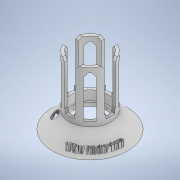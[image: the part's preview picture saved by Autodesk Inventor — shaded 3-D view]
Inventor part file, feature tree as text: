
AUTODESK INVENTOR PART (.ipt)
format: ipt  version: 2022.4 (Build 264492010, 492A)  size: 1,085,952 bytes
history: native  units: in
note: dims shown in document units (in); Inventor stores cm internally (conversion verified against a paired STEP export)
features: sketch x11, extrude x8, plane x3, pattern_circular x3, revolve x2, emboss x1
ambient origin geometry x8: Origin, YZ Plane, XZ Plane, XY Plane, X Axis, Y Axis, Z Axis, Center Point
bodies: Solid1 (feature_tree)
feature tree (28):
  extrude  "Extrusion1"  Depth=0.2559in
  plane  "Work Plane1"
  extrude  "Extrusion3"  Depth=2.3622in
  extrude  "Extrusion4"  TaperAngle=0.0deg  [1 undecoded]
  extrude  "Extrusion5"  Depth=2.2835in
  extrude  "Extrusion6"  Depth=0.1969in
  pattern_circular  "Circular Pattern2"  Count=10  [1 undecoded]
  extrude  "Extrusion7"  Depth=0.2559in
  revolve  "Revolution3"  Angle=360.0deg
  extrude  "Extrusion8"  TaperAngle=0.0deg  [1 undecoded]
  pattern_circular  "Circular Pattern4"  Count=7  [1 undecoded]
  emboss  "Emboss4"
  extrude  "Extrusion9"  Depth=0.1575in TaperAngle=0.0deg
  plane  "Work Plane5"
  sketch  "Sketch23"  dims[d54=3.248in d55=0.1575in d56=0.0in]
  plane  "Work Plane4"
  revolve  "Revolution5"  [1 undecoded]
  pattern_circular  "Circular Pattern5"  [2 undecoded]
  sketch  "Sketch1"  dims[d2=0.1969in d3=0.0in d10=0.2559in]
  sketch  "Sketch5"  dims[d11=2.5984in d12=2.3622in]
  sketch  "Sketch6"  dims[d13=0.1969in d14=0.0in d15=0.0in]
  sketch  "Sketch7"  dims[d16=2.5197in d17=2.2835in]
  sketch  "Sketch13"  dims[d18=0.0787in d19=0.0in d22=0.1969in d23=3.937in d24=0.0in]
  sketch  "Sketch14"  dims[d25=0.2559in d26=0.0in d40=3.7008in]
  sketch  "Sketch17"  dims[d43=0.0in d44=0.0in d45=3.1496in d46=360.0deg]
  sketch  "Sketch20"  dims[d49=0.5906in d50=0.0in]
  sketch  "Sketch21"  dims[d51=0.6299in d52=2.7559in]
  sketch  "Sketch24"  dims[d60=0.1969in d61=0.1969in d62=0.1969in d63=360.0deg d81=0.5906in d82=0.0in d83=0.7874in d85=0.0in d86=0.0in d87=1.5748in d88=360.0deg d98=0.0787in d102=0.315in d103=0.1969in d104=0.1969in d106=0.1969in d107=0.1969in d108=0.0787in d109=0.0in d110=0.315in d111=2.6772in d112=2.6772in d113=0.0787in d121=0.4331in d122=1.5748in d124=360.0deg d126=0.1378in d127=0.0in d130=135.0deg d137=90.0deg d138=0.1772in d139=1.5748in d140=360.0deg d68=0.0344in d69=0.0344in d72=0.0344in d73=0.0344in d131=0.0344in d132=0.0197in d133=0.0344in]
note: 7 required parameter values undecoded (feature->parameter linkage not recoverable at this tier; creation-order binding heuristic only, values carry confidence <= 0.55)